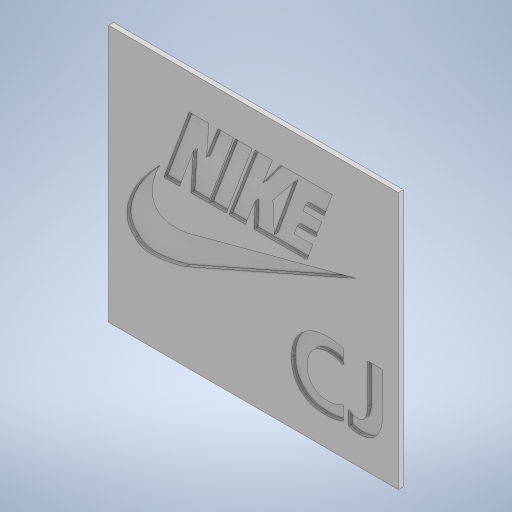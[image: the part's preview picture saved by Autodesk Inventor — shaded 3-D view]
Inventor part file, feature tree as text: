
AUTODESK INVENTOR PART (.ipt)
format: ipt  version: 2024.2 (Build 282272000, 272)  size: 375,808 bytes
history: native  units: mm
features: extrude x5, sketch x5, other x3
ambient origin geometry x8: Origin, YZ Plane, XZ Plane, XY Plane, X Axis, Y Axis, Z Axis, Center Point
bodies: Body1 (feature_tree)
feature tree (13):
  other  "Sólido1"
  extrude  "Extrusión1"  Depth=500.0mm
  extrude  "Extrusión4"  Depth=6.0mm
  extrude  "Extrusión5"  Depth=4.5mm TaperAngle=0.0deg
  extrude  "Extrusión6"  Depth=133.25mm TaperAngle=0.0deg
  extrude  "Extrusión7"  [1 undecoded]
  sketch  "Boceto1"  dims[d0=500.0mm d1=500.0mm]
  sketch  "Boceto4"  dims[d2=6.0mm d3=0.0mm d19=300.0mm]
  other  "Imagen2"
  sketch  "Boceto6"  dims[d29=4.5mm d30=0.0mm d31=4.5mm d32=0.0mm]
  sketch  "Boceto7"  dims[d40=4.5mm d41=0.0mm d42=133.25mm d43=0.0mm]
  other  "Imagen3"
  sketch  "Boceto8"
note: 1 required parameter value undecoded (feature->parameter linkage not recoverable at this tier; creation-order binding heuristic only, values carry confidence <= 0.55)
